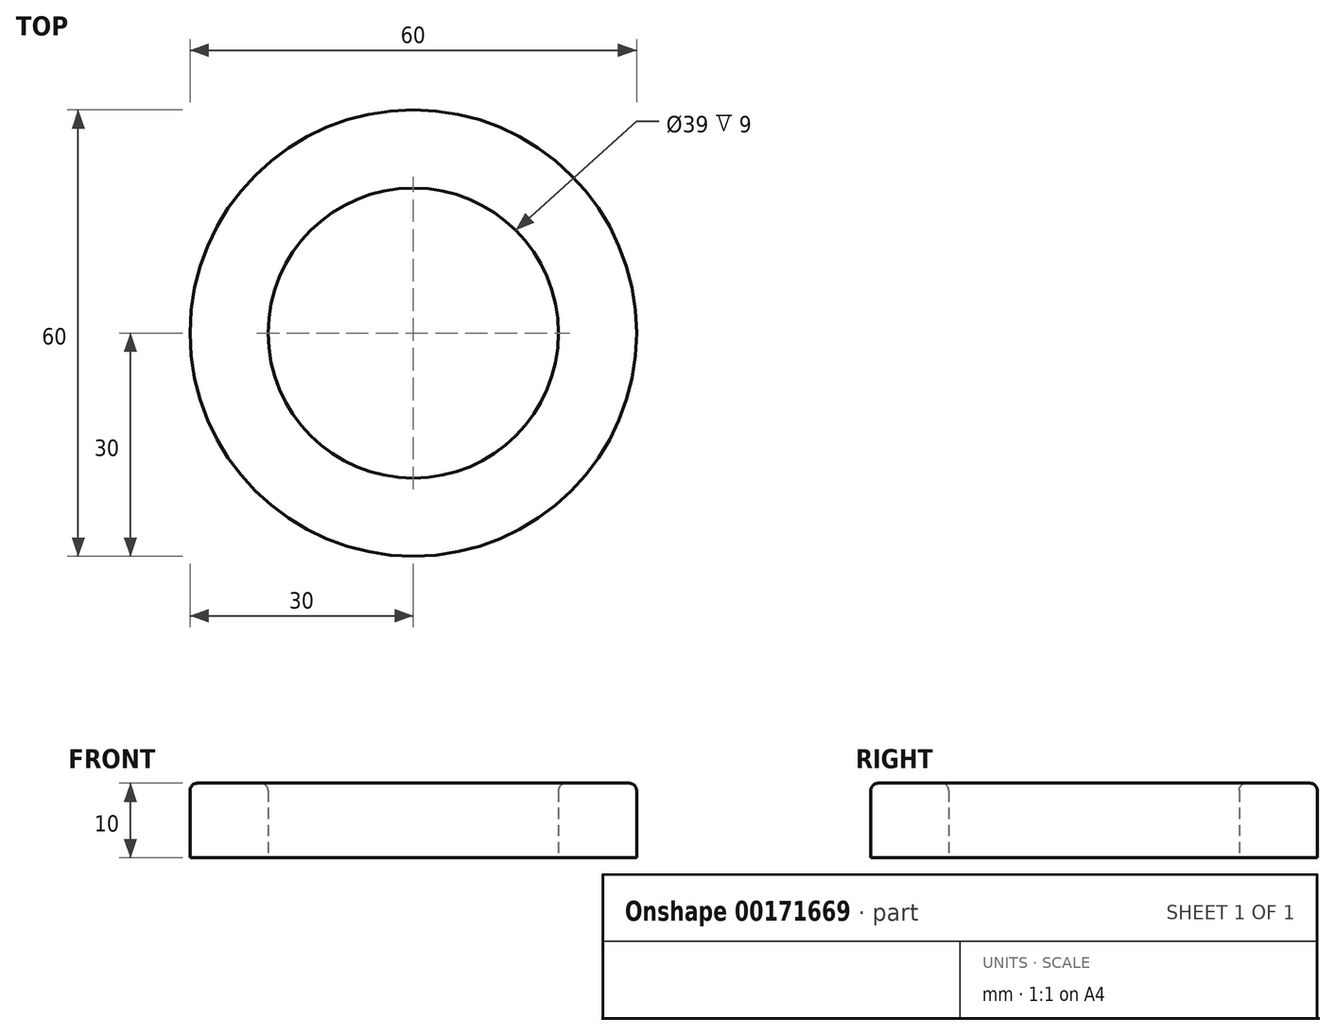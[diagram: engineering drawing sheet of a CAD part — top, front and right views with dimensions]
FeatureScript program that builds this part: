
annotation { "Feature Type Name" : "Feature", "Feature Type Description" : "" }
export const myFeature = defineFeature(function(context is Context, id is Id, definition is map)
    precondition{}
    {
        {
            var Q0;
            Q0=qCreatedBy(makeId("Top.planeOp"),FACE);
            var sketch = newSketch(context, id + "F0", { "sketchPlane" : qUnion([Q0])});
            skCircle(sketch, "E0", {"center": v(0, 0) * mm, "radius": 19.5 * mm});
            skCircle(sketch, "E1", {"center": v(0, 0) * mm, "radius": 30 * mm});
            skSolve(sketch);
        }
        {
            var Q0;
            Q0 = qSketchRegion(id + "F0", true);
            extrude(context, id + "F1", {"entities" : qUnion([Q0]), "depth" : 10 * mm});
        }
        {
            var Q0;
            Q0=makeQuery(id+"F1.opExtrude","CAP_EDGE",EDGE,{"disambiguationData":[OSD([sQuery(id+"F0.wireOp",EDGE,"E1")])],"isStart":false});
            var Q1;
            Q1=makeQuery(id+"F1.opExtrude","CAP_EDGE",EDGE,{"disambiguationData":[OSD([sQuery(id+"F0.wireOp",EDGE,"E0")])],"isStart":false});
            fillet(context, id + "F2", {"entities" : qUnion([Q0, Q1]), "radius" : 1 * mm, "tangentPropagation" : true, "allowEdgeOverflow" : false});
        }
    });
